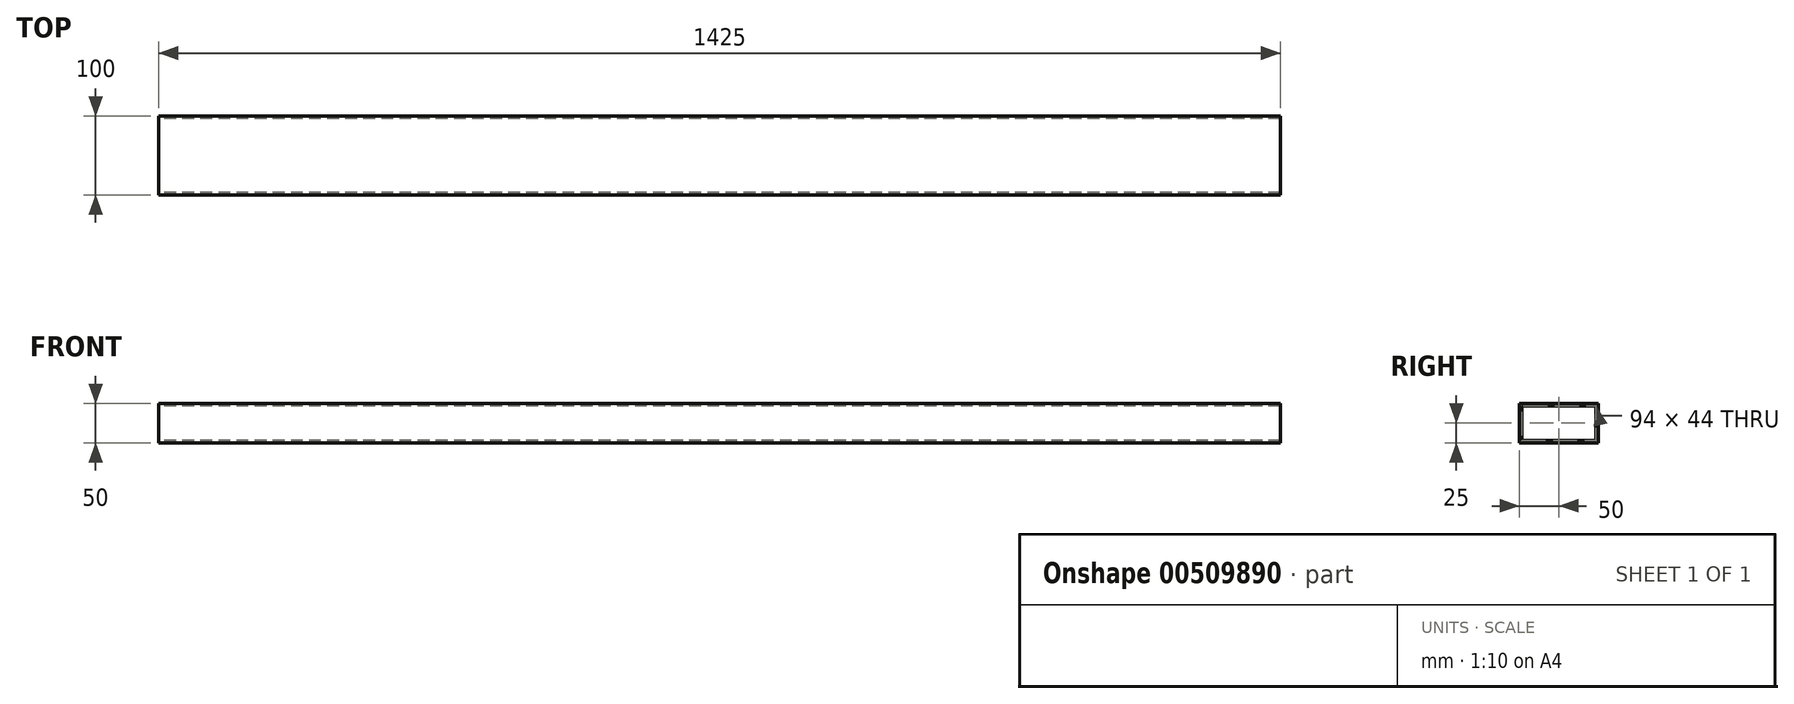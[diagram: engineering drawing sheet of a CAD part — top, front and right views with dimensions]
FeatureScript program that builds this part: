
annotation { "Feature Type Name" : "Feature", "Feature Type Description" : "" }
export const myFeature = defineFeature(function(context is Context, id is Id, definition is map)
    precondition{}
    {
        {
            var Q0;
            Q0=qCreatedBy(makeId("Right.planeOp"),FACE);
            var sketch = newSketch(context, id + "F0", { "sketchPlane" : qUnion([Q0])});
            skLineSegment(sketch, "E0.bottom", {"start": v(50, -25) * mm, "end": v(-50, -25) * mm});
            skLineSegment(sketch, "E0.top", {"start": v(50, 25) * mm, "end": v(-50, 25) * mm});
            skLineSegment(sketch, "E0.left", {"start": v(50, -25) * mm, "end": v(50, 25) * mm});
            skLineSegment(sketch, "E0.right", {"start": v(-50, -25) * mm, "end": v(-50, 25) * mm});
            skPoint(sketch, "E0.middle", {"position": v(0, 0) * mm});
            skLineSegment(sketch, "E1.bottom", {"start": v(47, -22) * mm, "end": v(-47, -22) * mm});
            skLineSegment(sketch, "E1.top", {"start": v(47, 22) * mm, "end": v(-47, 22) * mm});
            skLineSegment(sketch, "E1.left", {"start": v(47, -22) * mm, "end": v(47, 22) * mm});
            skLineSegment(sketch, "E1.right", {"start": v(-47, -22) * mm, "end": v(-47, 22) * mm});
            skSolve(sketch);
        }
        {
            var Q0;
            Q0=makeQuery(id+"F0.imprint","IMPRINT",FACE,{"disambiguationData":[TD([[makeQuery(id+"F0.imprint","IMPRINT",EDGE,{"derivedFrom":sQuery(id+"F0.wireOp",EDGE,"E0.bottom")}),-1.0]])]});
            extrude(context, id + "F1", {"entities" : qUnion([Q0]), "depth" : 1425 * mm, "offsetDistance" : 25 * mm});
        }
    });
